# Revit family: C8956- Slotted Pattern Linear Shower Drain - 48 inch
name_source: partatom
category: Generic Models
units: mm (PartAtom-declared; Revit-internal decimal feet)

## family parameters
Always vertical = Yes
Can host rebar = No
Cut with Voids When Loaded = No
Maintain Annotation Orientation = No
Part Type = Normal
Room Calculation Point = No
Round Connector Dimension = Use Diameter
Shared = No
Work Plane-Based = No

## types (1)
- C8956- Slotted Pattern Linear Shower Drain - 48"
    Default Elevation = 0 mm  [stored 0 ft]
    Fram Material = 4
    Gare Matel Material = 2
    Gare Material = 3
    Grove = 18
    Grove Width = 40 mm  [stored 0.131234 ft]
    Holder Material = 4
    Length = 1220 mm  [stored 4.00262 ft]
    Model = C8956
    URL = https://kromedispense.co.in
    Width = 70 mm  [stored 0.229659 ft]

note: [stored X ft] marks values corroborated as IEEE doubles in the binary element streams (Revit-internal decimal feet)

## geometry (parser evidence)
native form markers: Sweep x10
no freeform markers — native parametric forms only
